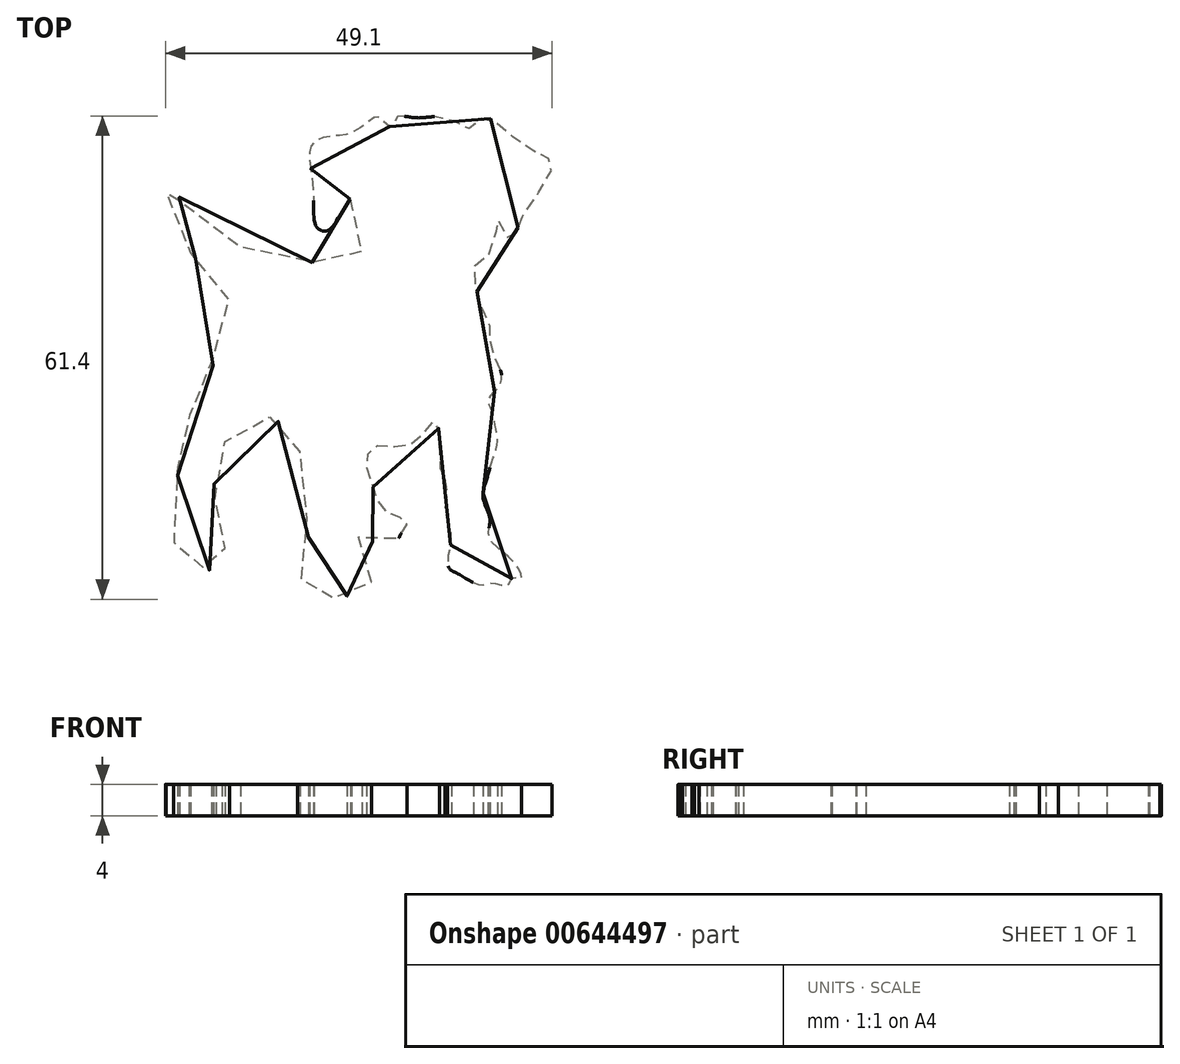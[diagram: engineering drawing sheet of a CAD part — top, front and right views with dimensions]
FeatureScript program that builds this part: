
annotation { "Feature Type Name" : "Feature", "Feature Type Description" : "" }
export const myFeature = defineFeature(function(context is Context, id is Id, definition is map)
    precondition{}
    {
        {
            var Q0;
            Q0=qCreatedBy(makeId("Top.planeOp"),FACE);
            var sketch = newSketch(context, id + "F0", { "sketchPlane" : qUnion([Q0])});
            skFitSpline(sketch, "E0", {"points": [v(25.78, 53.8) * mm, v(25.43, 50.81) * mm, v(25.9, 48.52) * mm, v(27.27, 46.9) * mm, v(26.35, 45.88) * mm, v(24.17, 45.65) * mm, v(20.96, 45.76) * mm, v(17.28, 45.07) * mm, v(11.77, 47.71) * mm, v(7.41, 50.47) * mm, v(4.43, 52.88) * mm, v(3.4, 56.9) * mm, v(2.48, 57.35) * mm, v(2.48, 54.94) * mm, v(2.48, 52.3) * mm, v(3.97, 49.32) * mm, v(7.3, 45.3) * mm, v(11.89, 42.32) * mm, v(9.36, 40.37) * mm, v(8.33, 38.19) * mm, v(8.22, 34.06) * mm, v(8.33, 31.76) * mm, v(7.07, 29.12) * mm, v(5.35, 26.02) * mm, v(5.46, 23.27) * mm, v(4.2, 21.09) * mm, v(3.86, 19.36) * mm, v(4.08, 14.31) * mm, v(3.4, 10.18) * mm, v(3.74, 8.12) * mm, v(5.58, 6.62) * mm, v(6.6, 7.2) * mm, v(7.87, 6.62) * mm, v(9.36, 7.31) * mm, v(10.17, 7.43) * mm, v(10.28, 9.03) * mm, v(8.8, 10.64) * mm, v(9.48, 12.13) * mm, v(8.9, 14.66) * mm, v(8.8, 18.56) * mm, v(10.28, 19.94) * mm, v(9.94, 23.15) * mm, v(11.89, 24.18) * mm, v(14.19, 26.82) * mm, v(16.14, 25.68) * mm, v(17.17, 25.56) * mm, v(19.12, 24.41) * mm, v(19.35, 21.32) * mm, v(19.7, 18.22) * mm, v(20.04, 14.43) * mm, v(20.38, 9.95) * mm, v(19.12, 7.08) * mm, v(19.58, 5.36) * mm, v(20.15, 3.52) * mm, v(21.53, 2.95) * mm, v(22.8, 3.3) * mm, v(24.86, 3.07) * mm, v(26.35, 3.87) * mm, v(27.84, 3.52) * mm, v(28.42, 5.6) * mm, v(26.35, 8.12) * mm, v(26.24, 11.21) * mm, v(27.38, 10.41) * mm, v(29, 10.41) * mm, v(29.45, 10.64) * mm, v(31.63, 10.3) * mm, v(32.2, 11.21) * mm, v(33, 12.36) * mm, v(32.32, 13.28) * mm, v(30.14, 14.2) * mm, v(28.65, 17.41) * mm, v(27.84, 20.51) * mm, v(28.88, 22.35) * mm, v(32.2, 22.35) * mm, v(34.84, 23.73) * mm, v(36.68, 25.56) * mm, v(37.14, 20.97) * mm, v(37.37, 19.13) * mm, v(38.06, 17.41) * mm, v(37.83, 14.08) * mm, v(38.29, 12.48) * mm, v(38.63, 10.41) * mm, v(38.29, 8.92) * mm, v(38.17, 7.43) * mm, v(38.63, 6.62) * mm, v(39.32, 6.28) * mm, v(42.3, 4.79) * mm, v(43.68, 5.02) * mm, v(45.86, 4.79) * mm, v(46.44, 5.7) * mm, v(47.47, 5.6) * mm, v(46.67, 7.54) * mm, v(43.45, 10.76) * mm, v(43.57, 12.82) * mm, v(43.1, 14.54) * mm, v(42.65, 16.04) * mm, v(43, 17.76) * mm, v(43.8, 20.4) * mm, v(44.49, 22.8) * mm, v(44.26, 24.76) * mm, v(43.68, 27.17) * mm, v(43.34, 28.32) * mm, v(44.83, 30.27) * mm, v(44.72, 32.56) * mm, v(43.91, 34.17) * mm, v(43.57, 36.58) * mm, v(43.34, 38.53) * mm, v(42.08, 40.6) * mm, v(41.85, 42.43) * mm, v(41.62, 45.3) * mm, v(43.91, 47.48) * mm, v(44.49, 51.27) * mm, v(45.75, 48.98) * mm, v(46.67, 49.1) * mm, v(47.47, 51.16) * mm, v(51.19, 57.01) * mm, v(51.19, 58.73) * mm, v(48.96, 60) * mm, v(44.75, 63.13) * mm, v(42.7, 64.12) * mm, v(40.8, 62.72) * mm, v(38.2, 64.12) * mm, v(34.24, 64.12) * mm, v(31.65, 64.12) * mm, v(31.24, 62.85) * mm, v(29.47, 64.12) * mm, v(28.82, 64.12) * mm, v(26.09, 62.26) * mm, v(24.04, 61.85) * mm, v(21.17, 61.03) * mm, v(20.63, 59.26) * mm, v(20.9, 56.66) * mm, v(21.17, 53.39) * mm, v(21.45, 50.38) * mm, v(22.54, 49.7) * mm, v(23.36, 50.11) * mm, v(24.31, 51.48) * mm, v(25.78, 53.8) * mm]});
            skSolve(sketch);
        }
        {
            var Q0;
            Q0 = qSketchRegion(id + "F0", true);
            extrude(context, id + "F1", {"entities" : qUnion([Q0]), "depth" : 4 * mm, "offsetDistance" : 25 * mm});
        }
    });
